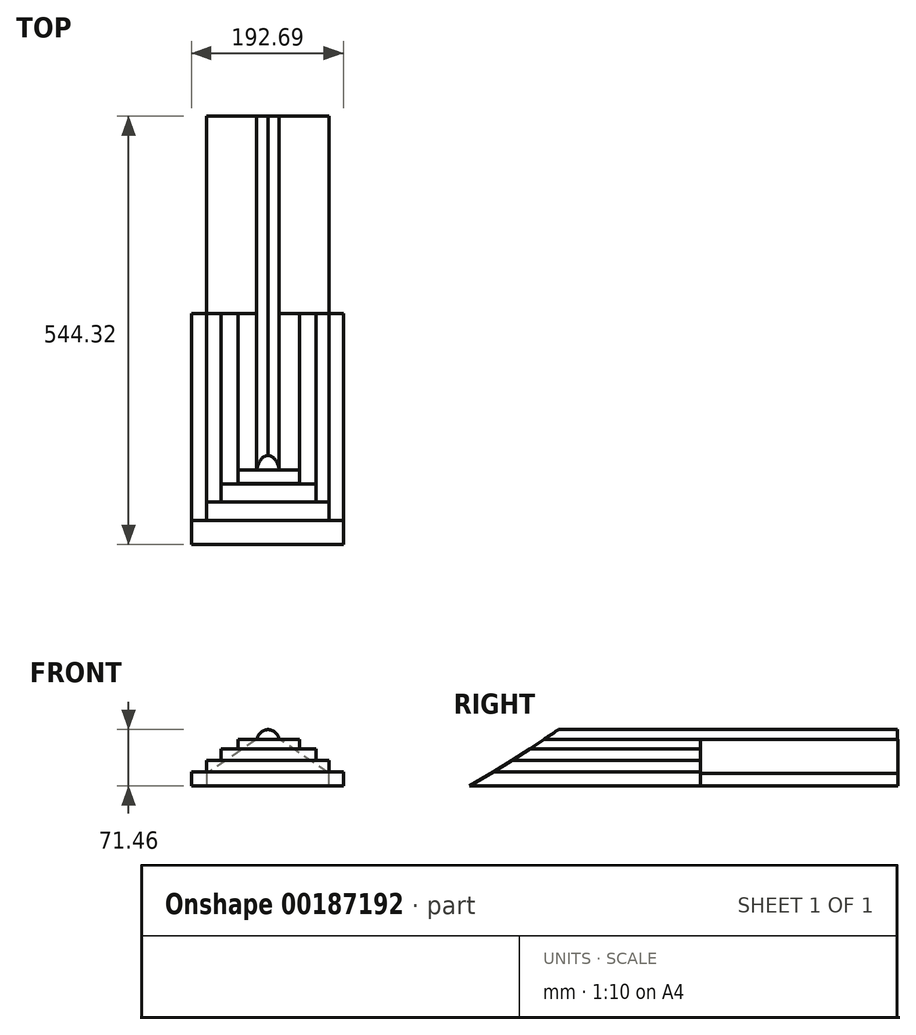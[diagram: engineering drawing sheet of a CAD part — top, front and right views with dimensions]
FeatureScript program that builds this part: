
annotation { "Feature Type Name" : "Feature", "Feature Type Description" : "" }
export const myFeature = defineFeature(function(context is Context, id is Id, definition is map)
    precondition{}
    {
        {
            var Q0;
            Q0=qCreatedBy(makeId("Front.planeOp"),FACE);
            var sketch = newSketch(context, id + "F0", { "sketchPlane" : qUnion([Q0])});
            skLineSegment(sketch, "E0.bottom", {"start": v(-93.52, -43.77) * mm, "end": v(99.17, -43.77) * mm});
            skLineSegment(sketch, "E0.top", {"start": v(-93.52, -26.15) * mm, "end": v(99.17, -26.15) * mm});
            skLineSegment(sketch, "E0.left", {"start": v(-93.52, -43.77) * mm, "end": v(-93.52, -26.15) * mm});
            skLineSegment(sketch, "E0.right", {"start": v(99.17, -43.77) * mm, "end": v(99.17, -26.15) * mm});
            skSolve(sketch);
        }
        {
            var Q0;
            Q0 = qSketchRegion(id + "F0", true);
            extrude(context, id + "F1", {"entities" : qUnion([Q0]), "depth" : 293.62 * mm});
        }
        {
            var Q0;
            Q0=makeQuery(id+"F1.opExtrude","CAP_EDGE",EDGE,{"disambiguationData":[OSD([sQuery(id+"F0.wireOp",EDGE,"E0.top")])],"isStart":false});
            chamfer(context, id + "F2", {"entities" : qUnion([Q0]), "chamferType" : ChamferType.OFFSET_ANGLE, "width" : 30.48 * mm, "oppositeDirection" : false, "angle" : 30 * degree, "tangentPropagation" : true});
        }
        {
            var Q0;
            Q0=makeQuery(id+"F1.opExtrude","CAP_FACE",FACE,{"disambiguationData":[OSD([sQuery(id+"F0.wireOp",EDGE,"E0.bottom"),sQuery(id+"F0.wireOp",EDGE,"E0.top"),sQuery(id+"F0.wireOp",EDGE,"E0.left"),sQuery(id+"F0.wireOp",EDGE,"E0.right")])],"isStart":true});
            var sketch = newSketch(context, id + "F3", { "sketchPlane" : qUnion([Q0])});
            skLineSegment(sketch, "E1.bottom", {"start": v(-80.99, -26.15) * mm, "end": v(74.56, -26.15) * mm});
            skLineSegment(sketch, "E1.top", {"start": v(-80.99, -11.37) * mm, "end": v(74.56, -11.37) * mm});
            skLineSegment(sketch, "E1.left", {"start": v(-80.99, -26.15) * mm, "end": v(-80.99, -11.37) * mm});
            skLineSegment(sketch, "E1.right", {"start": v(74.56, -26.15) * mm, "end": v(74.56, -11.37) * mm});
            skSolve(sketch);
        }
        {
            var Q0;
            Q0 = qSketchRegion(id + "F3", true);
            extrude(context, id + "F4", {"entities" : qUnion([Q0]), "operationType" : NewBodyOperationType.ADD, "oppositeDirection" : true, "depth" : 262.8 * mm});
        }
        {
            var Q0;
            Q0=makeQuery(id+"F4.opExtrude","CAP_EDGE",EDGE,{"disambiguationData":[OSD([sQuery(id+"F3.wireOp",EDGE,"E1.top")])],"isStart":false});
            chamfer(context, id + "F5", {"entities" : qUnion([Q0]), "chamferType" : ChamferType.OFFSET_ANGLE, "width" : 14.48 * mm, "oppositeDirection" : false, "angle" : 58 * degree, "tangentPropagation" : true});
        }
        {
            var Q0;
            Q0=makeQuery(id+"F4.boolean.opBoolean","MERGE",FACE,{"derivedFrom":[makeQuery(id+"F1.opExtrude","CAP_FACE",FACE,{"disambiguationData":[OSD([sQuery(id+"F0.wireOp",EDGE,"E0.bottom"),sQuery(id+"F0.wireOp",EDGE,"E0.top"),sQuery(id+"F0.wireOp",EDGE,"E0.left"),sQuery(id+"F0.wireOp",EDGE,"E0.right")])],"isStart":true}),makeQuery(id+"F4.opExtrude","CAP_FACE",FACE,{"disambiguationData":[OSD([sQuery(id+"F3.wireOp",EDGE,"E1.bottom"),sQuery(id+"F3.wireOp",EDGE,"E1.top"),sQuery(id+"F3.wireOp",EDGE,"E1.left"),sQuery(id+"F3.wireOp",EDGE,"E1.right")])],"isStart":true})]});
            var sketch = newSketch(context, id + "F6", { "sketchPlane" : qUnion([Q0])});
            skLineSegment(sketch, "E2.bottom", {"start": v(-64.27, -11.37) * mm, "end": v(56.09, -11.37) * mm});
            skLineSegment(sketch, "E2.top", {"start": v(-64.27, 3.01) * mm, "end": v(56.09, 3.01) * mm});
            skLineSegment(sketch, "E2.left", {"start": v(-64.27, -11.37) * mm, "end": v(-64.27, 3.01) * mm});
            skLineSegment(sketch, "E2.right", {"start": v(56.09, -11.37) * mm, "end": v(56.09, 3.01) * mm});
            skSolve(sketch);
        }
        {
            var Q0;
            Q0 = qSketchRegion(id + "F6", true);
            extrude(context, id + "F7", {"entities" : qUnion([Q0]), "operationType" : NewBodyOperationType.ADD, "oppositeDirection" : true, "depth" : 239.6 * mm});
        }
        {
            var Q0;
            Q0=makeQuery(id+"F7.opExtrude","CAP_EDGE",EDGE,{"disambiguationData":[OSD([sQuery(id+"F6.wireOp",EDGE,"E2.top")])],"isStart":false});
            chamfer(context, id + "F8", {"entities" : qUnion([Q0]), "chamferType" : ChamferType.OFFSET_ANGLE, "width" : 14.48 * mm, "oppositeDirection" : false, "angle" : 58 * degree, "tangentPropagation" : true});
        }
        {
            var Q0;
            Q0=makeQuery(id+"F7.boolean.opBoolean","MERGE",FACE,{"derivedFrom":[makeQuery(id+"F4.boolean.opBoolean","MERGE",FACE,{"derivedFrom":[makeQuery(id+"F1.opExtrude","CAP_FACE",FACE,{"disambiguationData":[OSD([sQuery(id+"F0.wireOp",EDGE,"E0.bottom"),sQuery(id+"F0.wireOp",EDGE,"E0.top"),sQuery(id+"F0.wireOp",EDGE,"E0.left"),sQuery(id+"F0.wireOp",EDGE,"E0.right")])],"isStart":true}),makeQuery(id+"F4.opExtrude","CAP_FACE",FACE,{"disambiguationData":[OSD([sQuery(id+"F3.wireOp",EDGE,"E1.bottom"),sQuery(id+"F3.wireOp",EDGE,"E1.top"),sQuery(id+"F3.wireOp",EDGE,"E1.left"),sQuery(id+"F3.wireOp",EDGE,"E1.right")])],"isStart":true})]}),makeQuery(id+"F7.opExtrude","CAP_FACE",FACE,{"disambiguationData":[OSD([sQuery(id+"F6.wireOp",EDGE,"E2.bottom"),sQuery(id+"F6.wireOp",EDGE,"E2.top"),sQuery(id+"F6.wireOp",EDGE,"E2.left"),sQuery(id+"F6.wireOp",EDGE,"E2.right")])],"isStart":true})]});
            var sketch = newSketch(context, id + "F9", { "sketchPlane" : qUnion([Q0])});
            skLineSegment(sketch, "E3.bottom", {"start": v(-43.27, 3.01) * mm, "end": v(34.7, 3.01) * mm});
            skLineSegment(sketch, "E3.top", {"start": v(-43.27, 15.26) * mm, "end": v(34.7, 15.26) * mm});
            skLineSegment(sketch, "E3.left", {"start": v(-43.27, 3.01) * mm, "end": v(-43.27, 15.26) * mm});
            skLineSegment(sketch, "E3.right", {"start": v(34.7, 3.01) * mm, "end": v(34.7, 15.26) * mm});
            skSolve(sketch);
        }
        {
            var Q0;
            Q0 = qSketchRegion(id + "F9", true);
            extrude(context, id + "F10", {"entities" : qUnion([Q0]), "operationType" : NewBodyOperationType.ADD, "oppositeDirection" : true, "depth" : 216.4 * mm});
        }
        {
            var Q0;
            Q0=makeQuery(id+"F10.opExtrude","CAP_EDGE",EDGE,{"disambiguationData":[OSD([sQuery(id+"F9.wireOp",EDGE,"E3.top")])],"isStart":false});
            chamfer(context, id + "F11", {"entities" : qUnion([Q0]), "chamferType" : ChamferType.OFFSET_ANGLE, "width" : 12.32 * mm, "oppositeDirection" : false, "angle" : 55 * degree, "tangentPropagation" : true});
        }
        {
            var Q0;
            Q0=makeQuery(id+"F10.boolean.opBoolean","MERGE",FACE,{"derivedFrom":[makeQuery(id+"F7.boolean.opBoolean","MERGE",FACE,{"derivedFrom":[makeQuery(id+"F4.boolean.opBoolean","MERGE",FACE,{"derivedFrom":[makeQuery(id+"F1.opExtrude","CAP_FACE",FACE,{"disambiguationData":[OSD([sQuery(id+"F0.wireOp",EDGE,"E0.bottom"),sQuery(id+"F0.wireOp",EDGE,"E0.top"),sQuery(id+"F0.wireOp",EDGE,"E0.left"),sQuery(id+"F0.wireOp",EDGE,"E0.right")])],"isStart":true}),makeQuery(id+"F4.opExtrude","CAP_FACE",FACE,{"disambiguationData":[OSD([sQuery(id+"F3.wireOp",EDGE,"E1.bottom"),sQuery(id+"F3.wireOp",EDGE,"E1.top"),sQuery(id+"F3.wireOp",EDGE,"E1.left"),sQuery(id+"F3.wireOp",EDGE,"E1.right")])],"isStart":true})]}),makeQuery(id+"F7.opExtrude","CAP_FACE",FACE,{"disambiguationData":[OSD([sQuery(id+"F6.wireOp",EDGE,"E2.bottom"),sQuery(id+"F6.wireOp",EDGE,"E2.top"),sQuery(id+"F6.wireOp",EDGE,"E2.left"),sQuery(id+"F6.wireOp",EDGE,"E2.right")])],"isStart":true})]}),makeQuery(id+"F10.opExtrude","CAP_FACE",FACE,{"disambiguationData":[OSD([sQuery(id+"F9.wireOp",EDGE,"E3.bottom"),sQuery(id+"F9.wireOp",EDGE,"E3.top"),sQuery(id+"F9.wireOp",EDGE,"E3.left"),sQuery(id+"F9.wireOp",EDGE,"E3.right")])],"isStart":true})]});
            var sketch = newSketch(context, id + "F12", { "sketchPlane" : qUnion([Q0])});
            skLineSegment(sketch, "E4.bottom", {"start": v(-17.8, 15.26) * mm, "end": v(10.79, 15.26) * mm});
            skLineSegment(sketch, "E4.top", {"start": v(-17.8, 27.7) * mm, "end": v(10.79, 27.7) * mm});
            skLineSegment(sketch, "E4.left", {"start": v(-17.8, 15.26) * mm, "end": v(-17.8, 27.7) * mm});
            skLineSegment(sketch, "E4.right", {"start": v(10.79, 15.26) * mm, "end": v(10.79, 27.7) * mm});
            skSolve(sketch);
        }
        {
            var Q0;
            Q0 = qSketchRegion(id + "F12", true);
            extrude(context, id + "F13", {"entities" : qUnion([Q0]), "operationType" : NewBodyOperationType.ADD, "oppositeDirection" : true, "depth" : 198.63 * mm});
        }
        {
            var Q0;
            Q0=makeQuery(id+"F13.opExtrude","CAP_EDGE",EDGE,{"disambiguationData":[OSD([sQuery(id+"F12.wireOp",EDGE,"E4.top")])],"isStart":false});
            chamfer(context, id + "F14", {"entities" : qUnion([Q0]), "chamferType" : ChamferType.OFFSET_ANGLE, "width" : 12.32 * mm, "oppositeDirection" : false, "angle" : 56 * degree, "tangentPropagation" : true});
        }
        {
            var Q0;
            Q0=makeQuery(id+"F13.opExtrude","SWEPT_EDGE",EDGE,{"disambiguationData":[OSD([sQuery(id+"F12.wireOp",EDGE,"E4.top"),sQuery(id+"F12.wireOp",EDGE,"E4.left")])]});
            var Q1;
            Q1=makeQuery(id+"F13.opExtrude","SWEPT_EDGE",EDGE,{"disambiguationData":[OSD([sQuery(id+"F12.wireOp",EDGE,"E4.top"),sQuery(id+"F12.wireOp",EDGE,"E4.right")])]});
            fillet(context, id + "F15", {"entities" : qUnion([Q0, Q1]), "radius" : 15.33 * mm, "tangentPropagation" : true, "allowEdgeOverflow" : false});
        }
        {
            var Q0;
            Q0=makeQuery(id+"F13.boolean.opBoolean","MERGE",FACE,{"derivedFrom":[makeQuery(id+"F10.boolean.opBoolean","MERGE",FACE,{"derivedFrom":[makeQuery(id+"F7.boolean.opBoolean","MERGE",FACE,{"derivedFrom":[makeQuery(id+"F4.boolean.opBoolean","MERGE",FACE,{"derivedFrom":[makeQuery(id+"F1.opExtrude","CAP_FACE",FACE,{"disambiguationData":[OSD([sQuery(id+"F0.wireOp",EDGE,"E0.bottom"),sQuery(id+"F0.wireOp",EDGE,"E0.top"),sQuery(id+"F0.wireOp",EDGE,"E0.left"),sQuery(id+"F0.wireOp",EDGE,"E0.right")])],"isStart":true}),makeQuery(id+"F4.opExtrude","CAP_FACE",FACE,{"disambiguationData":[OSD([sQuery(id+"F3.wireOp",EDGE,"E1.bottom"),sQuery(id+"F3.wireOp",EDGE,"E1.top"),sQuery(id+"F3.wireOp",EDGE,"E1.left"),sQuery(id+"F3.wireOp",EDGE,"E1.right")])],"isStart":true})]}),makeQuery(id+"F7.opExtrude","CAP_FACE",FACE,{"disambiguationData":[OSD([sQuery(id+"F6.wireOp",EDGE,"E2.bottom"),sQuery(id+"F6.wireOp",EDGE,"E2.top"),sQuery(id+"F6.wireOp",EDGE,"E2.left"),sQuery(id+"F6.wireOp",EDGE,"E2.right")])],"isStart":true})]}),makeQuery(id+"F10.opExtrude","CAP_FACE",FACE,{"disambiguationData":[OSD([sQuery(id+"F9.wireOp",EDGE,"E3.bottom"),sQuery(id+"F9.wireOp",EDGE,"E3.top"),sQuery(id+"F9.wireOp",EDGE,"E3.left"),sQuery(id+"F9.wireOp",EDGE,"E3.right")])],"isStart":true})]}),makeQuery(id+"F13.opExtrude","CAP_FACE",FACE,{"disambiguationData":[OSD([sQuery(id+"F12.wireOp",EDGE,"E4.bottom"),sQuery(id+"F12.wireOp",EDGE,"E4.top"),sQuery(id+"F12.wireOp",EDGE,"E4.left"),sQuery(id+"F12.wireOp",EDGE,"E4.right")])],"isStart":true})]});
            var sketch = newSketch(context, id + "F16", { "sketchPlane" : qUnion([Q0])});
            skLineSegment(sketch, "E5", {"start": v(-80.99, -43.77) * mm, "end": v(-80.99, -27.7) * mm});
            skLineSegment(sketch, "E6", {"start": v(-80.99, -27.7) * mm, "end": v(-17.8, 15.26) * mm});
            skLineSegment(sketch, "E7", {"start": v(-17.8, 15.26) * mm, "end": v(10.79, 15.26) * mm});
            skLineSegment(sketch, "E8", {"start": v(10.79, 15.26) * mm, "end": v(74.56, -28.48) * mm});
            skLineSegment(sketch, "E9", {"start": v(74.56, -28.48) * mm, "end": v(74.56, -43.77) * mm});
            skLineSegment(sketch, "E10", {"start": v(74.56, -43.77) * mm, "end": v(-80.99, -43.77) * mm});
            skSolve(sketch);
        }
        {
            var Q0;
            Q0 = qSketchRegion(id + "F16", true);
            extrude(context, id + "F17", {"entities" : qUnion([Q0]), "operationType" : NewBodyOperationType.ADD, "depth" : 250.7 * mm});
        }
        {
            var Q0;
            {var subQ0=sQuery(id+"F12.wireOp",EDGE,"E4.left");var subQ1=sQuery(id+"F12.wireOp",EDGE,"E4.top");var subQ2=sQuery(id+"F12.wireOp",EDGE,"E4.right");var subQ3=makeQuery(id+"F13.opExtrude","CAP_FACE",FACE,{"disambiguationData":[OSD([sQuery(id+"F12.wireOp",EDGE,"E4.bottom"),subQ1,subQ0,subQ2])],"isStart":true});var subQ4=sQuery(id+"F9.wireOp",EDGE,"E3.top");var subQ5=makeQuery(id+"F4.opExtrude","CAP_FACE",FACE,{"disambiguationData":[OSD([sQuery(id+"F3.wireOp",EDGE,"E1.bottom"),sQuery(id+"F3.wireOp",EDGE,"E1.top"),sQuery(id+"F3.wireOp",EDGE,"E1.left"),sQuery(id+"F3.wireOp",EDGE,"E1.right")])],"isStart":true});var subQ6=makeQuery(id+"F1.opExtrude","CAP_FACE",FACE,{"disambiguationData":[OSD([sQuery(id+"F0.wireOp",EDGE,"E0.bottom"),sQuery(id+"F0.wireOp",EDGE,"E0.top"),sQuery(id+"F0.wireOp",EDGE,"E0.left"),sQuery(id+"F0.wireOp",EDGE,"E0.right")])],"isStart":true});var subQ7=makeQuery(id+"F7.opExtrude","CAP_FACE",FACE,{"disambiguationData":[OSD([sQuery(id+"F6.wireOp",EDGE,"E2.bottom"),sQuery(id+"F6.wireOp",EDGE,"E2.top"),sQuery(id+"F6.wireOp",EDGE,"E2.left"),sQuery(id+"F6.wireOp",EDGE,"E2.right")])],"isStart":true});var subQ8=makeQuery(id+"F10.opExtrude","CAP_FACE",FACE,{"disambiguationData":[OSD([sQuery(id+"F9.wireOp",EDGE,"E3.bottom"),subQ4,sQuery(id+"F9.wireOp",EDGE,"E3.left"),sQuery(id+"F9.wireOp",EDGE,"E3.right")])],"isStart":true});Q0=makeQuery(id+"F17.boolean.opBoolean","SPLIT",FACE,{"disambiguationData":[TD([subQ6,subQ5,subQ7,subQ8,makeQuery(id+"F10.opExtrude","SWEPT_FACE",FACE,{"disambiguationData":[OSD([subQ4])]}),subQ3,makeQuery(id+"F15.opFillet","BLEND_FACE",FACE,{"disambiguationData":[OSD([subQ1,subQ0])]}),makeQuery(id+"F15.opFillet","BLEND_FACE",FACE,{"disambiguationData":[OSD([subQ1,subQ2])]}),makeQuery(id+"F17.opExtrude","SWEPT_FACE",FACE,{"disambiguationData":[OSD([sQuery(id+"F16.wireOp",EDGE,"E6")])]}),makeQuery(id+"F17.opExtrude","SWEPT_FACE",FACE,{"disambiguationData":[OSD([sQuery(id+"F16.wireOp",EDGE,"E7")])]}),makeQuery(id+"F17.opExtrude","SWEPT_FACE",FACE,{"disambiguationData":[OSD([sQuery(id+"F16.wireOp",EDGE,"E8")])]})])],"derivedFrom":makeQuery(id+"F13.boolean.opBoolean","MERGE",FACE,{"derivedFrom":[makeQuery(id+"F10.boolean.opBoolean","MERGE",FACE,{"derivedFrom":[makeQuery(id+"F7.boolean.opBoolean","MERGE",FACE,{"derivedFrom":[makeQuery(id+"F4.boolean.opBoolean","MERGE",FACE,{"derivedFrom":[subQ6,subQ5]}),subQ7]}),subQ8]}),subQ3]})});}
            extrude(context, id + "F18", {"entities" : qUnion([Q0]), "operationType" : NewBodyOperationType.ADD, "depth" : 250.44 * mm});
        }
    });
